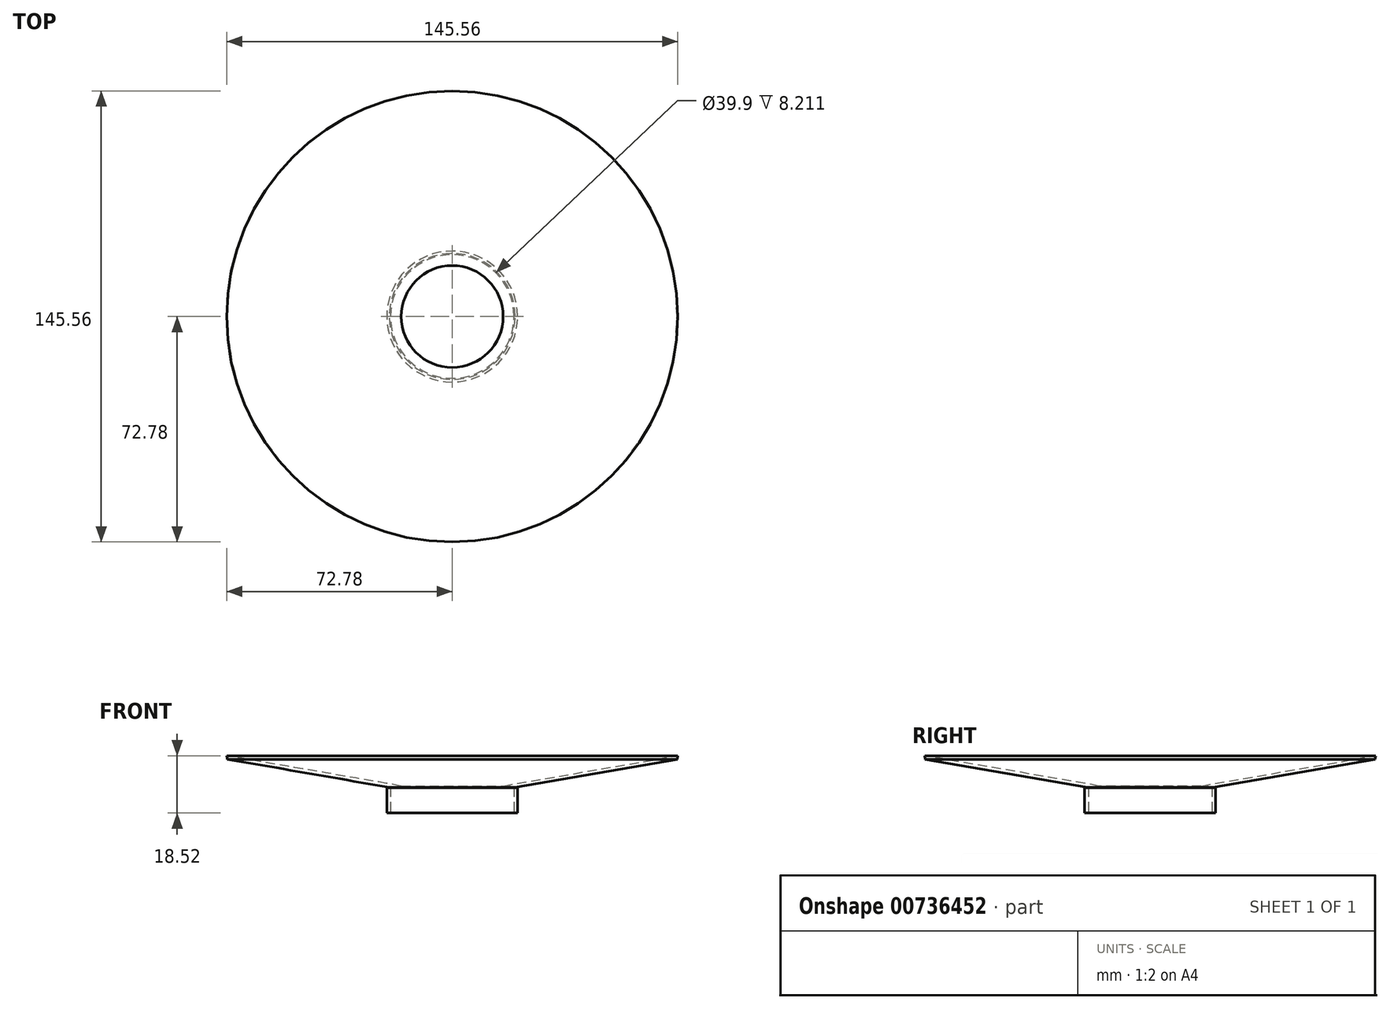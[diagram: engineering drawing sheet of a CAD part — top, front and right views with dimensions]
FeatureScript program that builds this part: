
annotation { "Feature Type Name" : "Feature", "Feature Type Description" : "" }
export const myFeature = defineFeature(function(context is Context, id is Id, definition is map)
    precondition{}
    {
        {
            var Q0;
            Q0=qCreatedBy(makeId("Front.planeOp"),FACE);
            var sketch = newSketch(context, id + "F0", { "sketchPlane" : qUnion([Q0])});
            skLineSegment(sketch, "E0.bottom", {"start": v(19.95, 0) * mm, "end": v(21.14, 0) * mm});
            skLineSegment(sketch, "E0.top", {"start": v(19.95, 8.21) * mm, "end": v(21.14, 8.21) * mm});
            skLineSegment(sketch, "E0.left", {"start": v(19.95, 0) * mm, "end": v(19.95, 8.21) * mm});
            skLineSegment(sketch, "E0.right", {"start": v(21.14, 0) * mm, "end": v(21.14, 8.21) * mm});
            skSolve(sketch);
        }
        {
            var Q0;
            Q0=qCreatedBy(makeId("Front.planeOp"),FACE);
            var sketch = newSketch(context, id + "F1", { "sketchPlane" : qUnion([Q0])});
            skLineSegment(sketch, "E1", {"start": v(0, 0) * mm, "end": v(0, 29.27) * mm});
            skSolve(sketch);
        }
        {
            var Q0;
            Q0 = qSketchRegion(id + "F0", true);
            var Q1;
            Q1=sQuery(id+"F1.wireOp",EDGE,"E1");
            revolve(context, id + "F2", {"surfaceOperationType" : NewSurfaceOperationType.NEW, "entities" : qUnion([Q0]), "axis" : qUnion([Q1]), "revolveType" : RevolveType.FULL});
        }
        {
            var Q0;
            Q0=qCreatedBy(makeId("Front.planeOp"),FACE);
            var sketch = newSketch(context, id + "F3", { "sketchPlane" : qUnion([Q0])});
            skLineSegment(sketch, "E2", {"start": v(20.33, 8.3) * mm, "end": v(72.6, 17.37) * mm});
            skLineSegment(sketch, "E3", {"start": v(16.45, 8.75) * mm, "end": v(72.78, 18.52) * mm});
            skLineSegment(sketch, "E4", {"start": v(72.6, 17.37) * mm, "end": v(72.78, 18.52) * mm});
            skFitSpline(sketch, "E5", {"points": [v(20.33, 8.3) * mm, v(16.45, 8.75) * mm, v(0, 9.6) * mm], "startDerivative": vector(-9.8, 1.4) * mm, "endDerivative": vector(-28.7, 1.24) * mm});
            skSolve(sketch);
        }
        {
            var Q0;
            Q0 = qSketchRegion(id + "F3", true);
            var Q1;
            Q1=sQuery(id+"F1.wireOp",EDGE,"E1");
            revolve(context, id + "F4", {"surfaceOperationType" : NewSurfaceOperationType.NEW, "entities" : qUnion([Q0]), "axis" : qUnion([Q1]), "revolveType" : RevolveType.FULL});
        }
        {
            var Q0;
            Q0=sQuery(id+"F3.wireOp",EDGE,"Gyt0tzH7-9CWN-SCqZ-Adtw-rTvbKuS1BpkP");
            var Q1;
            Q1=sQuery(id+"F3.wireOp",EDGE,"E5");
            var Q2;
            Q2=sQuery(id+"F1.wireOp",EDGE,"E1");
            revolve(context, id + "F5", {"bodyType" : ToolBodyType.SURFACE, "surfaceOperationType" : NewSurfaceOperationType.NEW, "surfaceEntities" : qUnion([Q0, Q1]), "axis" : qUnion([Q2]), "revolveType" : RevolveType.FULL});
        }
    });
